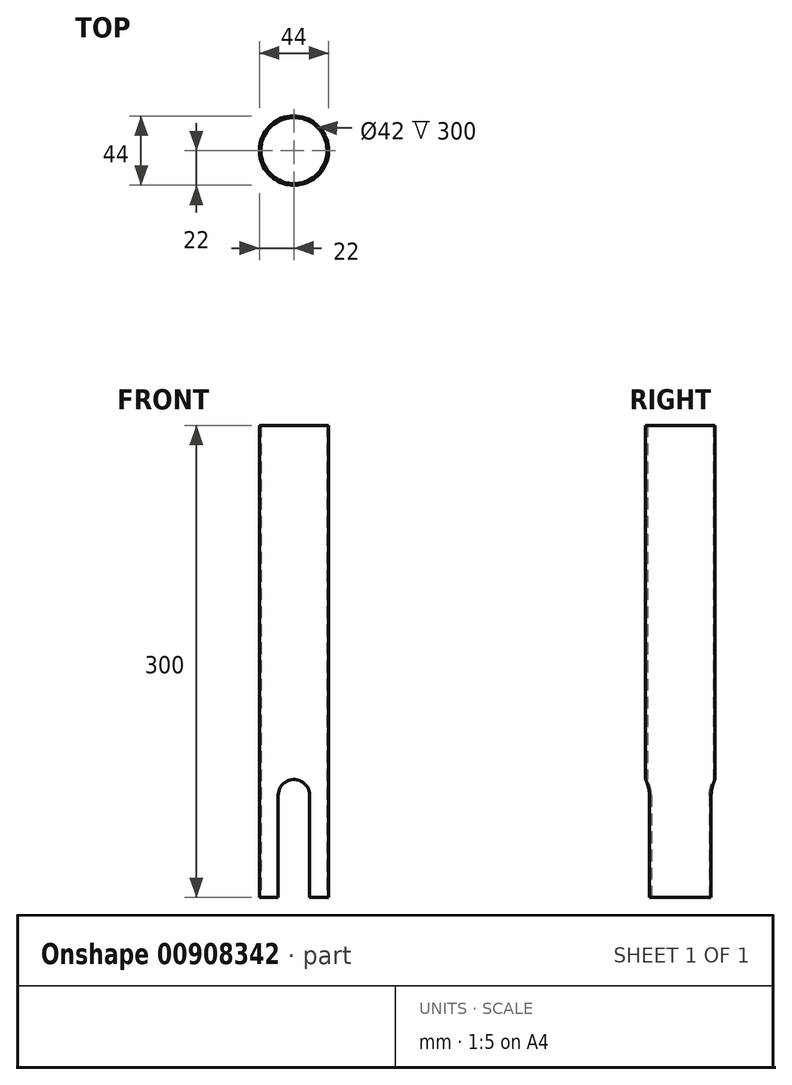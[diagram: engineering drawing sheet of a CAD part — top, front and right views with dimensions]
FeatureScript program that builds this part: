
annotation { "Feature Type Name" : "Feature", "Feature Type Description" : "" }
export const myFeature = defineFeature(function(context is Context, id is Id, definition is map)
    precondition{}
    {
        {
            var Q0;
            Q0=qCreatedBy(makeId("Top.planeOp"),FACE);
            var sketch = newSketch(context, id + "F0", { "sketchPlane" : qUnion([Q0])});
            skCircle(sketch, "E0", {"center": v(0, 0) * mm, "radius": 22 * mm});
            skCircle(sketch, "E1", {"center": v(0, 0) * mm, "radius": 21 * mm});
            skSolve(sketch);
        }
        {
            var Q0;
            Q0=makeQuery(id+"F0.imprint","IMPRINT",FACE,{"disambiguationData":[TD([[makeQuery(id+"F0.imprint","IMPRINT",EDGE,{"derivedFrom":sQuery(id+"F0.wireOp",EDGE,"E0")}),1.0]])]});
            extrude(context, id + "F1", {"entities" : qUnion([Q0]), "depth" : 300 * mm, "offsetDistance" : 25 * mm});
        }
        {
            var Q0;
            Q0=qCreatedBy(makeId("Front.planeOp"),FACE);
            var sketch = newSketch(context, id + "F2", { "sketchPlane" : qUnion([Q0])});
            skPoint(sketch, "E2", {"position": v(10, 0) * mm});
            skPoint(sketch, "E3", {"position": v(-10, 0) * mm});
            skLineSegment(sketch, "E4.bottom", {"start": v(-10, 0) * mm, "end": v(10, 0) * mm});
            skLineSegment(sketch, "E4.top", {"start": v(-10, 65) * mm, "end": v(10, 65) * mm});
            skLineSegment(sketch, "E4.left", {"start": v(-10, 0) * mm, "end": v(-10, 65) * mm});
            skLineSegment(sketch, "E4.right", {"start": v(10, 0) * mm, "end": v(10, 65) * mm});
            skCircle(sketch, "E5", {"center": v(0, 65) * mm, "radius": 10 * mm});
            skSolve(sketch);
        }
        {
            var Q0;
            Q0 = qSketchRegion(id + "F2", true);
            var Q1;
            Q1=sQuery(id+"F2.wireOp",EDGE,"E4.right");
            var Q2;
            Q2=sQuery(id+"F2.wireOp",EDGE,"E5");
            var Q3;
            Q3=sQuery(id+"F2.wireOp",EDGE,"E4.left");
            var Q4;
            Q4=sQuery(id+"F2.wireOp",EDGE,"E4.bottom");
            extrude(context, id + "F3", {"entities" : qUnion([Q0]), "operationType" : NewBodyOperationType.REMOVE, "surfaceEntities" : qUnion([Q1, Q2, Q3, Q4]), "endBound" : BoundingType.SYMMETRIC, "depth" : 100 * mm, "offsetDistance" : 25 * mm});
        }
    });
